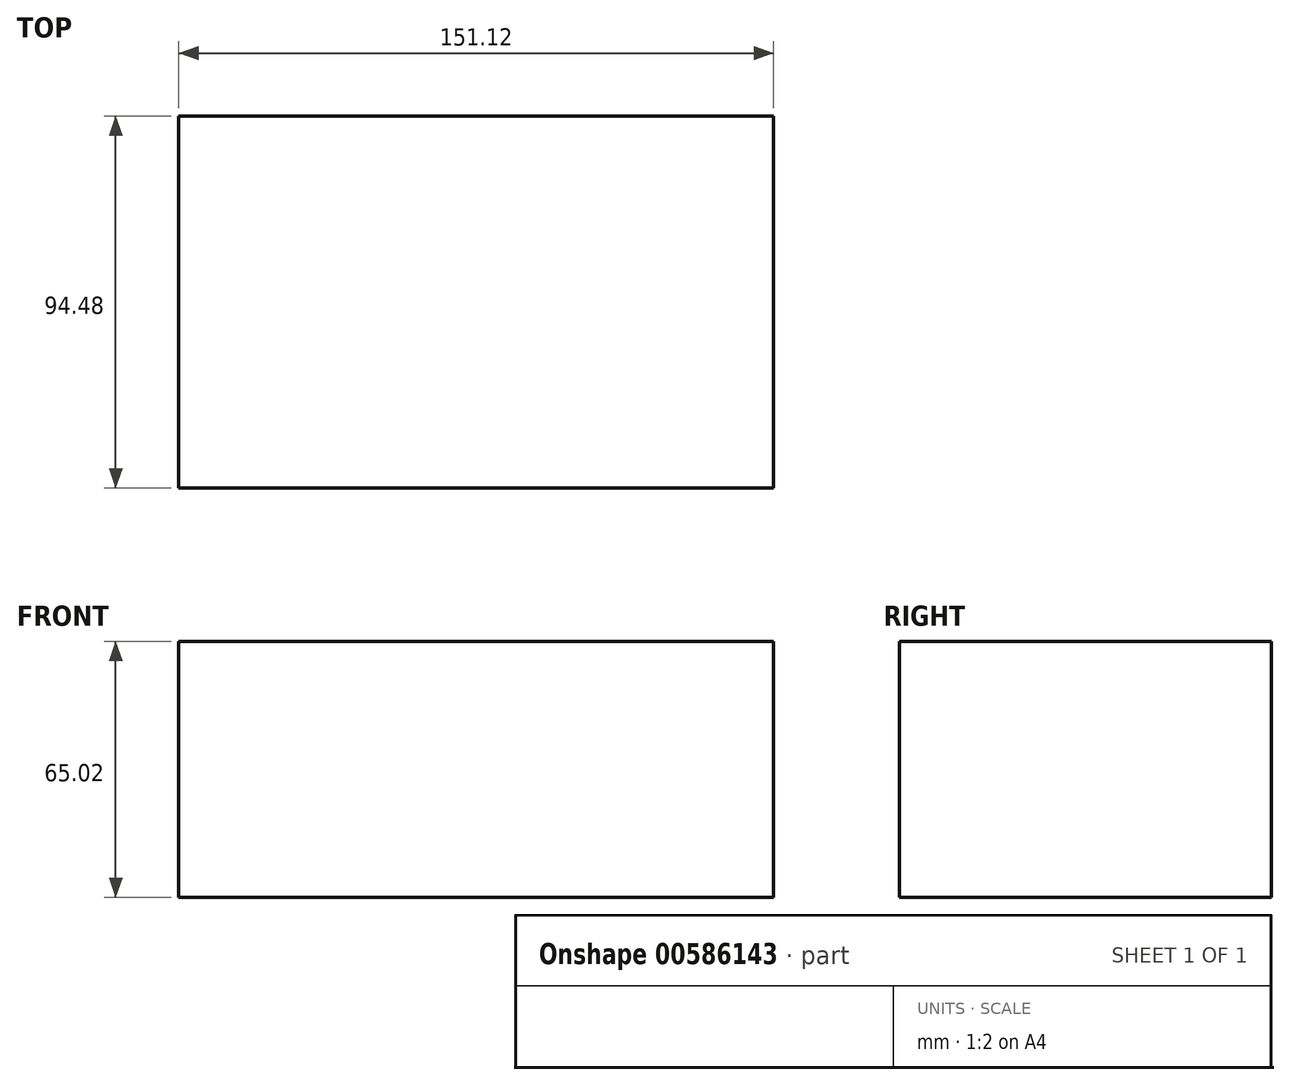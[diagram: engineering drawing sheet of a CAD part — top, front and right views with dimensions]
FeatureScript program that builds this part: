
annotation { "Feature Type Name" : "Feature", "Feature Type Description" : "" }
export const myFeature = defineFeature(function(context is Context, id is Id, definition is map)
    precondition{}
    {
        {
            var Q0;
            Q0=qCreatedBy(makeId("Top.planeOp"),FACE);
            var sketch = newSketch(context, id + "F0", { "sketchPlane" : qUnion([Q0])});
            skLineSegment(sketch, "E0.bottom", {"start": v(-75.56, 47.24) * mm, "end": v(75.57, 47.24) * mm});
            skLineSegment(sketch, "E0.top", {"start": v(-75.57, -47.24) * mm, "end": v(75.56, -47.24) * mm});
            skLineSegment(sketch, "E0.left", {"start": v(-75.56, 47.24) * mm, "end": v(-75.57, -47.24) * mm});
            skLineSegment(sketch, "E0.right", {"start": v(75.57, 47.24) * mm, "end": v(75.56, -47.24) * mm});
            skPoint(sketch, "E0.middle", {"position": v(0, 0) * mm});
            skSolve(sketch);
        }
        {
            var Q0;
            Q0=makeQuery(id+"F0.imprint","IMPRINT",FACE,{"disambiguationData":[TD([[makeQuery(id+"F0.imprint","IMPRINT",EDGE,{"derivedFrom":sQuery(id+"F0.wireOp",EDGE,"E0.bottom")}),-1.0]])]});
            extrude(context, id + "F1", {"entities" : qUnion([Q0]), "depth" : 65.02 * mm, "offsetDistance" : 25.4 * mm});
        }
    });
